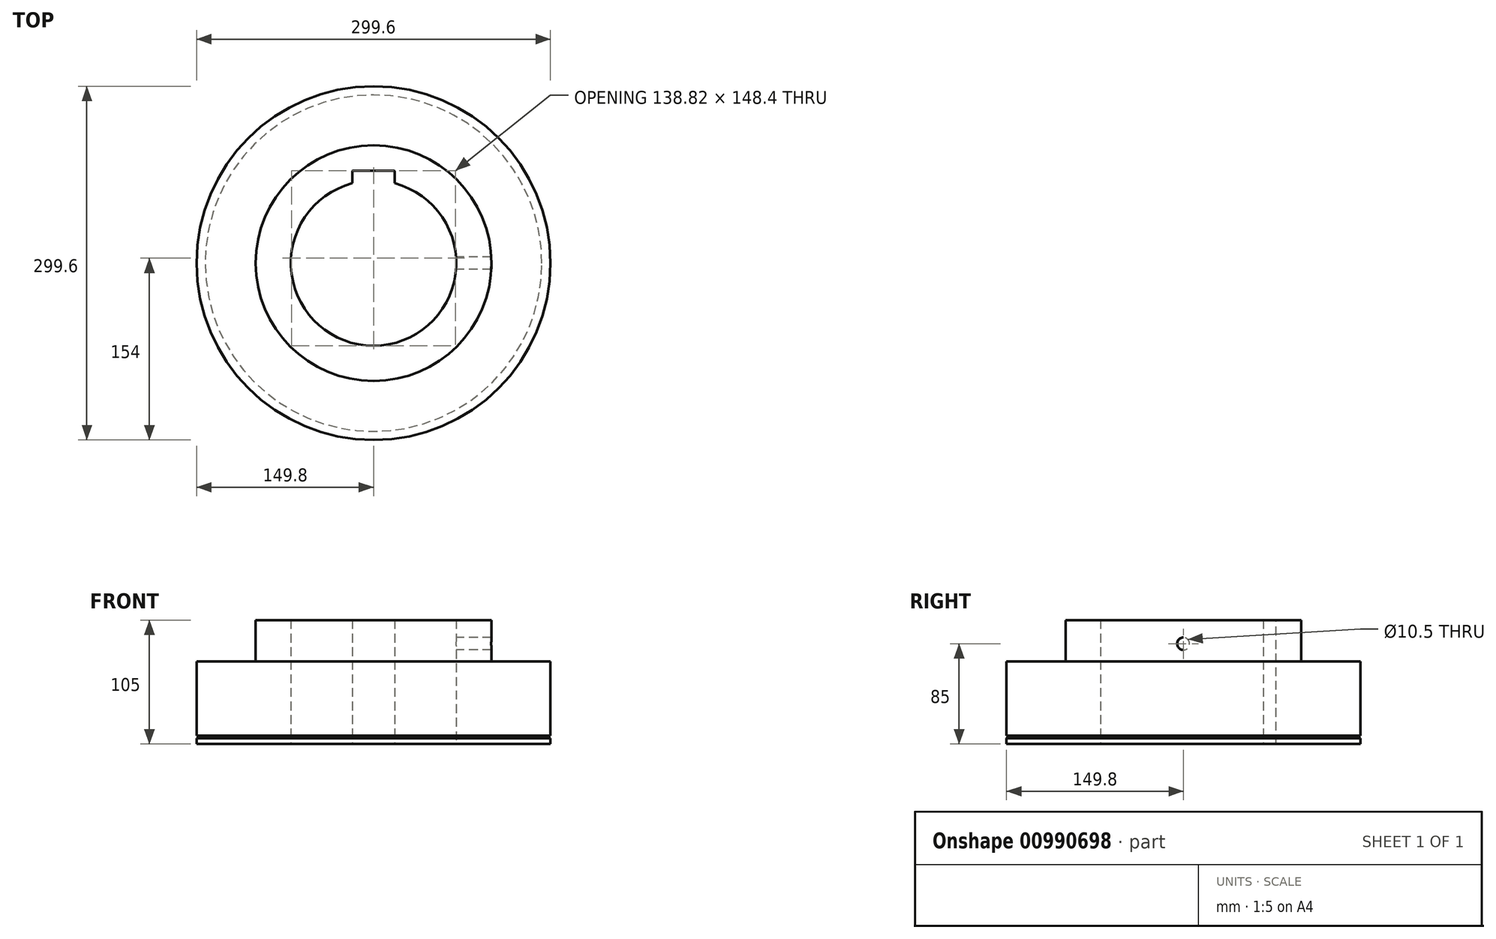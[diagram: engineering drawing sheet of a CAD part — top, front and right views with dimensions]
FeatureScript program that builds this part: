
annotation { "Feature Type Name" : "Feature", "Feature Type Description" : "" }
export const myFeature = defineFeature(function(context is Context, id is Id, definition is map)
    precondition{}
    {
        {
            var Q0;
            Q0=qCreatedBy(makeId("Top.planeOp"),FACE);
            var sketch = newSketch(context, id + "F0", { "sketchPlane" : qUnion([Q0])});
            skCircle(sketch, "E0", {"center": v(0, 0) * mm, "radius": 149.8 * mm});
            skCircle(sketch, "E1", {"center": v(0, 0) * mm, "radius": 99.8 * mm});
            skCircle(sketch, "E2", {"center": v(0, 0) * mm, "radius": 70 * mm});
            skSolve(sketch);
        }
        {
            var Q0;
            Q0=makeQuery(id+"F0.imprint","IMPRINT",FACE,{"disambiguationData":[TD([[makeQuery(id+"F0.imprint","IMPRINT",EDGE,{"derivedFrom":sQuery(id+"F0.wireOp",EDGE,"E0")}),1.0]])]});
            extrude(context, id + "F1", {"entities" : qUnion([Q0]), "depth" : 70 * mm, "offsetDistance" : 25 * mm});
        }
        {
            var Q0;
            Q0=makeQuery(id+"F0.imprint","IMPRINT",FACE,{"disambiguationData":[TD([[makeQuery(id+"F0.imprint","IMPRINT",EDGE,{"derivedFrom":sQuery(id+"F0.wireOp",EDGE,"E1")}),1.0]])]});
            extrude(context, id + "F2", {"entities" : qUnion([Q0]), "operationType" : NewBodyOperationType.ADD, "depth" : 105 * mm, "offsetDistance" : 25 * mm});
        }
        {
            var Q0;
            Q0=qCreatedBy(makeId("Right.planeOp"),FACE);
            var sketch = newSketch(context, id + "F3", { "sketchPlane" : qUnion([Q0])});
            skLineSegment(sketch, "E3", {"start": v(-149.8, 65) * mm, "end": v(-149.8, 5) * mm});
            skLineSegment(sketch, "E4", {"start": v(-149.8, 5) * mm, "end": v(-142.5, 7) * mm});
            skLineSegment(sketch, "E5", {"start": v(-142.5, 7) * mm, "end": v(-142.5, 63) * mm});
            skLineSegment(sketch, "E6", {"start": v(-142.5, 63) * mm, "end": v(-149.8, 65) * mm});
            skLineSegment(sketch, "E7", {"start": v(-142.5, 7) * mm, "end": v(-149.8, 7) * mm});
            skLineSegment(sketch, "E8", {"start": v(-149.8, 7) * mm, "end": v(-149.8, 5) * mm});
            skSolve(sketch);
        }
        {
            var Q0;
            Q0=makeQuery(id+"F3.imprint","IMPRINT",FACE,{"disambiguationData":[TD([[makeQuery(id+"F3.imprint","IMPRINT",EDGE,{"derivedFrom":sQuery(id+"F3.wireOp",EDGE,"E4")}),1.0]])]});
            var Q1;
            Q1=makeQuery(id+"F3.imprint","IMPRINT",FACE,{"disambiguationData":[TD([[makeQuery(id+"F3.imprint","IMPRINT",EDGE,{"derivedFrom":sQuery(id+"F3.wireOp",EDGE,"E3")}),1.0]])]});
            var Q2;
            Q2=makeQuery(id+"F1.opExtrude","CAP_EDGE",EDGE,{"disambiguationData":[OSD([sQuery(id+"F0.wireOp",EDGE,"E0")])],"isStart":false});
            sweep(context, id + "F4", {"operationType" : NewBodyOperationType.REMOVE, "profiles" : qUnion([Q0, Q1]), "path" : qUnion([Q2])});
        }
        {
            var Q0;
            Q0=qCreatedBy(makeId("Front.planeOp"),FACE);
            var sketch = newSketch(context, id + "F5", { "sketchPlane" : qUnion([Q0])});
            skLineSegment(sketch, "E9", {"start": v(18, -125) * mm, "end": v(0, -125) * mm});
            skLineSegment(sketch, "E10", {"start": v(0, -125) * mm, "end": v(-18, -125) * mm});
            skLineSegment(sketch, "E11", {"start": v(18, 125) * mm, "end": v(-18, 125) * mm});
            skLineSegment(sketch, "E12", {"start": v(18, 125) * mm, "end": v(18, -125) * mm});
            skLineSegment(sketch, "E13", {"start": v(-18, -125) * mm, "end": v(-18, 125) * mm});
            skLineSegment(sketch, "E14", {"start": v(18, 125) * mm, "end": v(-18, -125) * mm});
            skLineSegment(sketch, "E15", {"start": v(18, -125) * mm, "end": v(-18, 125) * mm});
            skSolve(sketch);
        }
        {
            var Q0;
            {var subQ0=sQuery(id+"F5.wireOp",EDGE,"E13");Q0=makeQuery(id+"F5.imprint","IMPRINT",FACE,{"disambiguationData":[TD([[makeQuery(id+"F5.imprint","IMPRINT",EDGE,{"derivedFrom":subQ0}),-1.0]])]});}
            var Q1;
            {var subQ0=sQuery(id+"F5.wireOp",EDGE,"E9");Q1=makeQuery(id+"F5.imprint","IMPRINT",FACE,{"disambiguationData":[TD([[makeQuery(id+"F5.imprint","IMPRINT",EDGE,{"derivedFrom":subQ0}),-1.0]])]});}
            var Q2;
            {var subQ0=sQuery(id+"F5.wireOp",EDGE,"E12");Q2=makeQuery(id+"F5.imprint","IMPRINT",FACE,{"disambiguationData":[TD([[makeQuery(id+"F5.imprint","IMPRINT",EDGE,{"derivedFrom":subQ0}),-1.0]])]});}
            var Q3;
            {var subQ0=sQuery(id+"F5.wireOp",EDGE,"E11");Q3=makeQuery(id+"F5.imprint","IMPRINT",FACE,{"disambiguationData":[TD([[makeQuery(id+"F5.imprint","IMPRINT",EDGE,{"derivedFrom":subQ0}),1.0]])]});}
            extrude(context, id + "F6", {"entities" : qUnion([Q0, Q1, Q2, Q3]), "operationType" : NewBodyOperationType.REMOVE, "oppositeDirection" : true, "depth" : 78.4 * mm, "offsetDistance" : 25 * mm});
        }
        {
            var Q0;
            Q0=qCreatedBy(makeId("Right.planeOp"),FACE);
            var sketch = newSketch(context, id + "F7", { "sketchPlane" : qUnion([Q0])});
            skCircle(sketch, "E16", {"center": v(0, 85) * mm, "radius": 7.07 * mm});
            skSolve(sketch);
        }
        {
            var Q0;
            Q0=sQuery(id+"F7.wireOp",VERTEX,"E16.center");
            var Q1;
            Q1=makeQuery(id+"F1.opExtrude","SWEPT_BODY",BODY,{"disambiguationData":[OSD([sQuery(id+"F0.wireOp",EDGE,"E0"),sQuery(id+"F0.wireOp",EDGE,"E1")])]});
            hole(context, id + "F8", {"style" : HoleStyle.SIMPLE, "endStyle" : HoleEndStyle.THROUGH, "oppositeDirection" : true, "standardTappedOrClearance" : lookupTablePath({ "standard" : "ISO", "engagement" : "75%", "pitch" : "1.5 mm", "size" : "M12", "type" : "Tapped" }), "standardBlindInLast" : lookupTablePath({ "standard" : "ISO", "fit" : "Normal", "engagement" : "75%", "pitch" : "1.5 mm", "size" : "M12", "type" : "Clearance & tapped" }), "holeDiameter" : 10.5 * mm, "majorDiameter" : 12 * mm, "showTappedDepth" : true, "isTappedThrough" : true, "tappedDepth" : 12 * mm, "tapClearance" : 3, "locations" : qUnion([Q0]), "scope" : qUnion([Q1])});
        }
        {
            var Q0;
            Q0=makeQuery(id+"F6.boolean.opBoolean","COPY",EDGE,{"derivedFrom":makeQuery(id+"F6.opExtrude","CAP_EDGE",EDGE,{"disambiguationData":[OSD([sQuery(id+"F5.wireOp",EDGE,"E12")])],"isStart":false})});
            var Q1;
            Q1=makeQuery(id+"F6.boolean.opBoolean","COPY",EDGE,{"derivedFrom":makeQuery(id+"F6.opExtrude","CAP_EDGE",EDGE,{"disambiguationData":[OSD([sQuery(id+"F5.wireOp",EDGE,"E13")])],"isStart":false})});
            fillet(context, id + "F9", {"entities" : qUnion([Q0, Q1]), "radius" : 0.8 * mm, "tangentPropagation" : true, "allowEdgeOverflow" : false});
        }
    });
